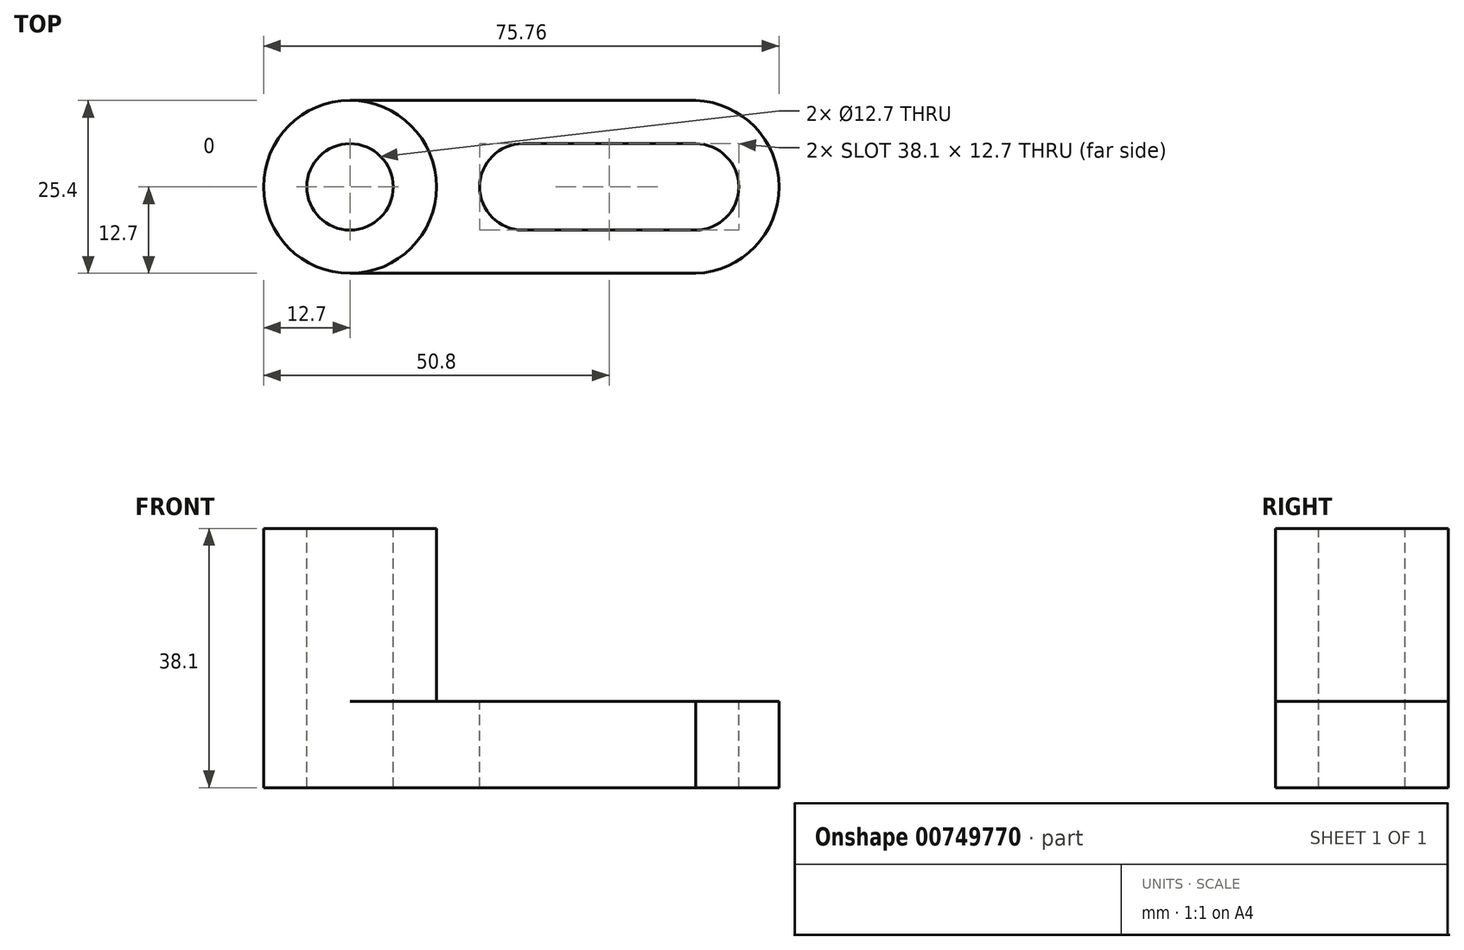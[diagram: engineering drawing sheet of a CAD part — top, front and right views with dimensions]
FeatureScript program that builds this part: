
annotation { "Feature Type Name" : "Feature", "Feature Type Description" : "" }
export const myFeature = defineFeature(function(context is Context, id is Id, definition is map)
    precondition{}
    {
        {
            var Q0;
            Q0=qCreatedBy(makeId("Front.planeOp"),FACE);
            var sketch = newSketch(context, id + "F0", { "sketchPlane" : qUnion([Q0])});
            skLineSegment(sketch, "E0", {"start": v(0, 0) * mm, "end": v(76.2, 0) * mm});
            skLineSegment(sketch, "E1", {"start": v(76.2, 0) * mm, "end": v(76.2, 12.7) * mm});
            skLineSegment(sketch, "E2", {"start": v(76.2, 12.7) * mm, "end": v(25.4, 12.7) * mm});
            skLineSegment(sketch, "E3", {"start": v(25.4, 12.7) * mm, "end": v(25.4, 38.1) * mm});
            skLineSegment(sketch, "E4", {"start": v(25.4, 38.1) * mm, "end": v(0, 38.1) * mm});
            skLineSegment(sketch, "E5", {"start": v(0, 38.1) * mm, "end": v(0, 0) * mm});
            skSolve(sketch);
        }
        {
            var Q0;
            Q0 = qSketchRegion(id + "F0", true);
            extrude(context, id + "F1", {"entities" : qUnion([Q0]), "depth" : 25.4 * mm, "offsetDistance" : 25.4 * mm});
        }
        {
            var Q0;
            Q0=makeQuery(id+"F1.opExtrude","SWEPT_FACE",FACE,{"disambiguationData":[OSD([sQuery(id+"F0.wireOp",EDGE,"E2")])]});
            var sketch = newSketch(context, id + "F2", { "sketchPlane" : qUnion([Q0])});
            skLineSegment(sketch, "E6", {"start": v(63.5, 0) * mm, "end": v(63.5, -25.4) * mm});
            skLineSegment(sketch, "E7", {"start": v(38.1, 0) * mm, "end": v(38.1, -25.4) * mm});
            skCircle(sketch, "E8", {"center": v(38.1, -12.7) * mm, "radius": 6.35 * mm});
            skCircle(sketch, "E9", {"center": v(63.5, -12.7) * mm, "radius": 6.35 * mm});
            skLineSegment(sketch, "E10", {"start": v(38.1, -6.35) * mm, "end": v(63.5, -6.35) * mm});
            skLineSegment(sketch, "E11", {"start": v(38.1, -19.05) * mm, "end": v(63.5, -19.05) * mm});
            skArc(sketch, "E12", {"start": v(63.5, -25.4) * mm, "mid": v(75.76, -12.7) * mm, "end": v(63.5, 0) * mm});
            skSolve(sketch);
        }
        {
            var Q0;
            {var subQ0=sQuery(id+"F2.wireOp",EDGE,"E12");Q0=makeQuery(id+"F2.imprint","IMPRINT",FACE,{"disambiguationData":[TD([[makeQuery(id+"F2.imprint","IMPRINT",EDGE,{"derivedFrom":subQ0}),-1.0]])]});}
            var Q1;
            {var subQ0=sQuery(id+"F2.wireOp",EDGE,"E9");var subQ1=sQuery(id+"F2.wireOp",EDGE,"E6");var subQ2=makeQuery(id+"F2.imprint","INTERSECT",VERTEX,{"derivedFrom":[subQ1,subQ0,sQuery(id+"F2.wireOp",EDGE,"E10")]});Q1=makeQuery(id+"F2.imprint","IMPRINT",FACE,{"disambiguationData":[TD([[makeQuery(id+"F2.imprint","IMPRINT",EDGE,{"disambiguationData":[TD([[subQ2,-1.0]])],"derivedFrom":subQ1}),1.0]])]});}
            var Q2;
            {var subQ0=sQuery(id+"F2.wireOp",EDGE,"E9");var subQ1=sQuery(id+"F2.wireOp",EDGE,"E6");var subQ2=makeQuery(id+"F2.imprint","INTERSECT",VERTEX,{"derivedFrom":[subQ1,subQ0,sQuery(id+"F2.wireOp",EDGE,"E10")]});Q2=makeQuery(id+"F2.imprint","IMPRINT",FACE,{"disambiguationData":[TD([[makeQuery(id+"F2.imprint","IMPRINT",EDGE,{"disambiguationData":[TD([[subQ2,-1.0]])],"derivedFrom":subQ1}),-1.0]])]});}
            var Q3;
            {var subQ0=sQuery(id+"F2.wireOp",EDGE,"E10");Q3=makeQuery(id+"F2.imprint","IMPRINT",FACE,{"disambiguationData":[TD([[makeQuery(id+"F2.imprint","IMPRINT",EDGE,{"derivedFrom":subQ0}),-1.0]])]});}
            var Q4;
            {var subQ0=sQuery(id+"F2.wireOp",EDGE,"E8");var subQ1=sQuery(id+"F2.wireOp",EDGE,"E7");var subQ2=makeQuery(id+"F2.imprint","INTERSECT",VERTEX,{"derivedFrom":[subQ1,subQ0,sQuery(id+"F2.wireOp",EDGE,"E10")]});Q4=makeQuery(id+"F2.imprint","IMPRINT",FACE,{"disambiguationData":[TD([[makeQuery(id+"F2.imprint","IMPRINT",EDGE,{"disambiguationData":[TD([[subQ2,-1.0]])],"derivedFrom":subQ1}),-1.0]])]});}
            var Q5;
            {var subQ0=sQuery(id+"F2.wireOp",EDGE,"E8");var subQ1=sQuery(id+"F2.wireOp",EDGE,"E7");var subQ2=makeQuery(id+"F2.imprint","INTERSECT",VERTEX,{"derivedFrom":[subQ1,subQ0,sQuery(id+"F2.wireOp",EDGE,"E10")]});Q5=makeQuery(id+"F2.imprint","IMPRINT",FACE,{"disambiguationData":[TD([[makeQuery(id+"F2.imprint","IMPRINT",EDGE,{"disambiguationData":[TD([[subQ2,-1.0]])],"derivedFrom":subQ1}),1.0]])]});}
            extrude(context, id + "F3", {"entities" : qUnion([Q0, Q1, Q2, Q3, Q4, Q5]), "operationType" : NewBodyOperationType.REMOVE, "endBound" : BoundingType.THROUGH_ALL, "oppositeDirection" : true, "depth" : 25.4 * mm, "offsetDistance" : 25.4 * mm});
        }
        {
            var Q0;
            Q0=makeQuery(id+"F1.opExtrude","SWEPT_FACE",FACE,{"disambiguationData":[OSD([sQuery(id+"F0.wireOp",EDGE,"E4")])]});
            var sketch = newSketch(context, id + "F4", { "sketchPlane" : qUnion([Q0])});
            skLineSegment(sketch, "E13", {"start": v(0, -12.7) * mm, "end": v(25.4, -12.7) * mm});
            skCircle(sketch, "E14", {"center": v(12.7, -12.7) * mm, "radius": 12.7 * mm});
            skCircle(sketch, "E15", {"center": v(12.7, -12.7) * mm, "radius": 6.35 * mm});
            skSolve(sketch);
        }
        {
            var Q0;
            {var subQ0=sQuery(id+"F4.wireOp",EDGE,"E14");var subQ1=sQuery(id+"F0.wireOp",EDGE,"E4");var subQ4=makeQuery(id+"F1.opExtrude","CAP_EDGE",EDGE,{"disambiguationData":[OSD([subQ1])],"isStart":true});var subQ5=makeQuery(id+"F4.imprint","INTERSECT",VERTEX,{"derivedFrom":[subQ4,subQ0]});Q0=makeQuery(id+"F4.imprint","IMPRINT",FACE,{"disambiguationData":[TD([[makeQuery(id+"F4.imprint","IMPRINT",EDGE,{"disambiguationData":[TD([[subQ5,-1.0]])],"derivedFrom":subQ4}),1.0]])]});}
            var Q1;
            {var subQ0=sQuery(id+"F4.wireOp",EDGE,"E14");var subQ1=sQuery(id+"F0.wireOp",EDGE,"E4");var subQ4=makeQuery(id+"F1.opExtrude","CAP_EDGE",EDGE,{"disambiguationData":[OSD([subQ1])],"isStart":false});var subQ5=makeQuery(id+"F4.imprint","INTERSECT",VERTEX,{"derivedFrom":[subQ4,subQ0]});Q1=makeQuery(id+"F4.imprint","IMPRINT",FACE,{"disambiguationData":[TD([[makeQuery(id+"F4.imprint","IMPRINT",EDGE,{"disambiguationData":[TD([[subQ5,-1.0]])],"derivedFrom":subQ4}),-1.0]])]});}
            var Q2;
            {var subQ0=sQuery(id+"F4.wireOp",EDGE,"E15");var subQ1=sQuery(id+"F4.wireOp",EDGE,"E13");var subQ2=makeQuery(id+"F4.imprint","INTERSECT",VERTEX,{"disambiguationData":[OD(0.0)],"derivedFrom":[subQ1,subQ0]});Q2=makeQuery(id+"F4.imprint","IMPRINT",FACE,{"disambiguationData":[TD([[makeQuery(id+"F4.imprint","IMPRINT",EDGE,{"disambiguationData":[TD([[subQ2,-1.0]])],"derivedFrom":subQ1}),-1.0]])]});}
            var Q3;
            {var subQ0=sQuery(id+"F4.wireOp",EDGE,"E15");var subQ1=sQuery(id+"F4.wireOp",EDGE,"E13");var subQ2=makeQuery(id+"F4.imprint","INTERSECT",VERTEX,{"disambiguationData":[OD(0.0)],"derivedFrom":[subQ1,subQ0]});Q3=makeQuery(id+"F4.imprint","IMPRINT",FACE,{"disambiguationData":[TD([[makeQuery(id+"F4.imprint","IMPRINT",EDGE,{"disambiguationData":[TD([[subQ2,-1.0]])],"derivedFrom":subQ1}),1.0]])]});}
            extrude(context, id + "F5", {"entities" : qUnion([Q0, Q1, Q2, Q3]), "operationType" : NewBodyOperationType.REMOVE, "endBound" : BoundingType.THROUGH_ALL, "oppositeDirection" : true, "depth" : 25.4 * mm, "offsetDistance" : 25.4 * mm});
        }
        {
            var Q0;
            Q0=makeQuery(id+"F1.opExtrude","SWEPT_FACE",FACE,{"disambiguationData":[OSD([sQuery(id+"F0.wireOp",EDGE,"E4")])]});
            var sketch = newSketch(context, id + "F6", { "sketchPlane" : qUnion([Q0])});
            skCircle(sketch, "E16", {"center": v(12.7, -12.7) * mm, "radius": 12.7 * mm});
            skSolve(sketch);
        }
        {
            var Q0;
            {var subQ1=sQuery(id+"F0.wireOp",EDGE,"E4");var subQ2=makeQuery(id+"F1.opExtrude","CAP_EDGE",EDGE,{"disambiguationData":[OSD([subQ1])],"isStart":true});Q0=makeQuery(id+"F6.imprint","IMPRINT",FACE,{"disambiguationData":[TD([[makeQuery(id+"F6.imprint","IMPRINT",EDGE,{"derivedFrom":subQ2}),1.0]])]});}
            var Q1;
            {var subQ1=sQuery(id+"F0.wireOp",EDGE,"E4");var subQ2=makeQuery(id+"F1.opExtrude","CAP_EDGE",EDGE,{"disambiguationData":[OSD([subQ1])],"isStart":false});Q1=makeQuery(id+"F6.imprint","IMPRINT",FACE,{"disambiguationData":[TD([[makeQuery(id+"F6.imprint","IMPRINT",EDGE,{"derivedFrom":subQ2}),-1.0]])]});}
            extrude(context, id + "F7", {"entities" : qUnion([Q0, Q1]), "operationType" : NewBodyOperationType.REMOVE, "oppositeDirection" : true, "depth" : 25.4 * mm, "offsetDistance" : 25.4 * mm});
        }
    });
